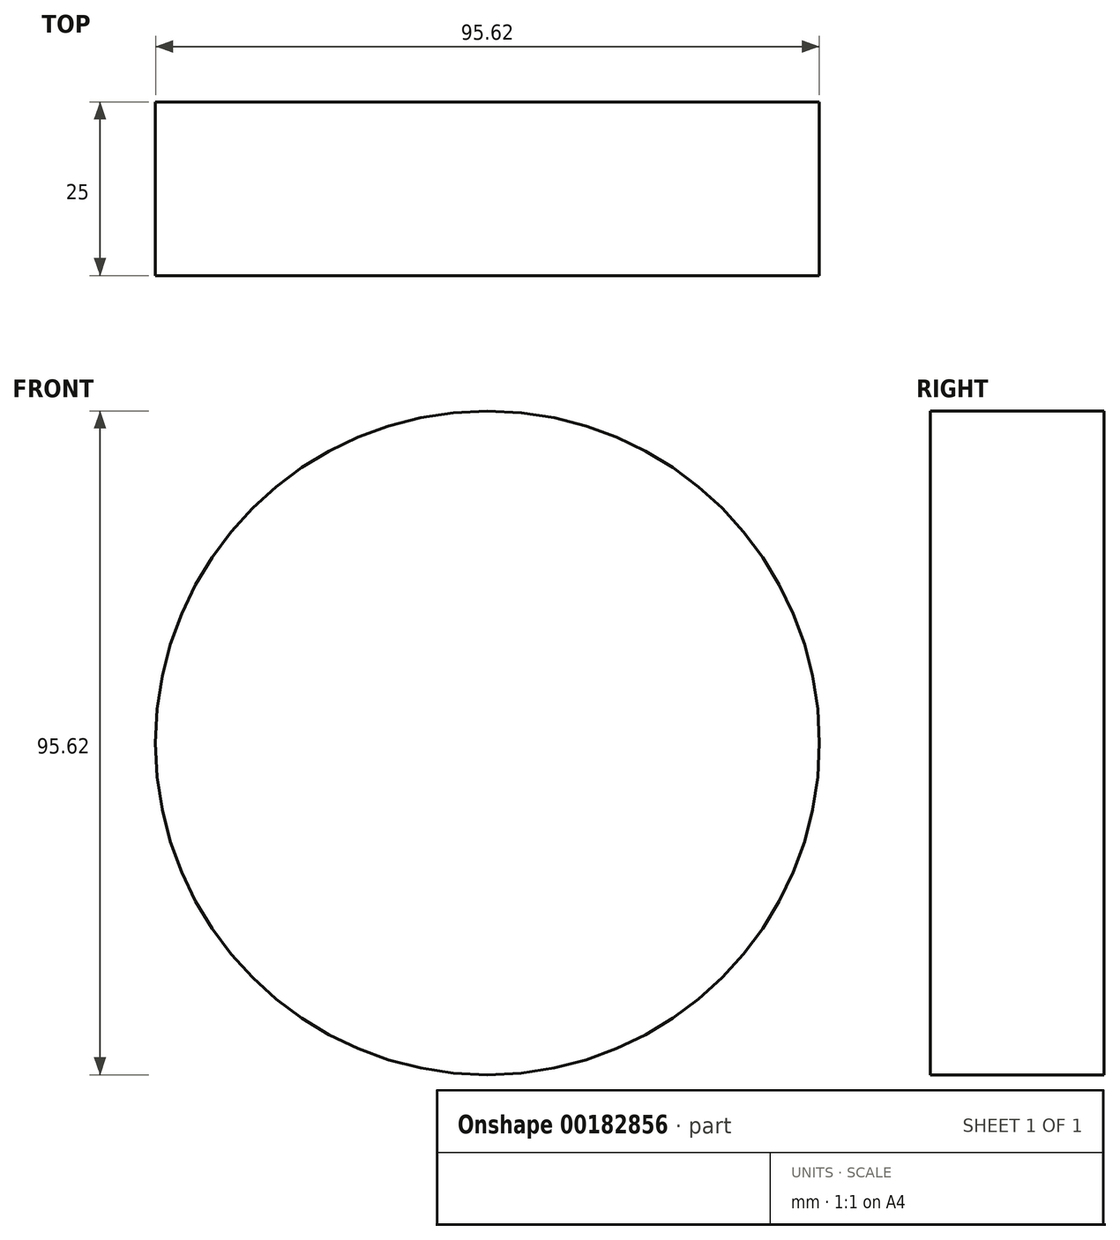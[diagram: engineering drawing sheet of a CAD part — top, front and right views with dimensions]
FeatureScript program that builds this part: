
annotation { "Feature Type Name" : "Feature", "Feature Type Description" : "" }
export const myFeature = defineFeature(function(context is Context, id is Id, definition is map)
    precondition{}
    {
        {
            var Q0;
            Q0=qCreatedBy(makeId("Front.planeOp"),FACE);
            var sketch = newSketch(context, id + "F0", { "sketchPlane" : qUnion([Q0])});
            skCircle(sketch, "E0", {"center": v(0, 0) * mm, "radius": 47.81 * mm});
            skSolve(sketch);
        }
        {
            var Q0;
            Q0 = qSketchRegion(id + "F0", true);
            extrude(context, id + "F1", {"entities" : qUnion([Q0]), "depth" : 25 * mm});
        }
        {
            var Q0;
            Q0=qCreatedBy(makeId("Front.planeOp"),FACE);
            var sketch = newSketch(context, id + "F2", { "sketchPlane" : qUnion([Q0])});
            skCircle(sketch, "E1", {"center": v(0, 22.43) * mm, "radius": 9.1 * mm});
            skCircle(sketch, "E2", {"center": v(0, 22.43) * mm, "radius": 10.19 * mm});
            skSolve(sketch);
        }
        {
            var Q0;
            Q0 = qSketchRegion(id + "F2", true);
            extrude(context, id + "F3", {"entities" : qUnion([Q0]), "operationType" : NewBodyOperationType.REMOVE, "oppositeDirection" : true, "depth" : 72.9 * mm});
        }
    });
